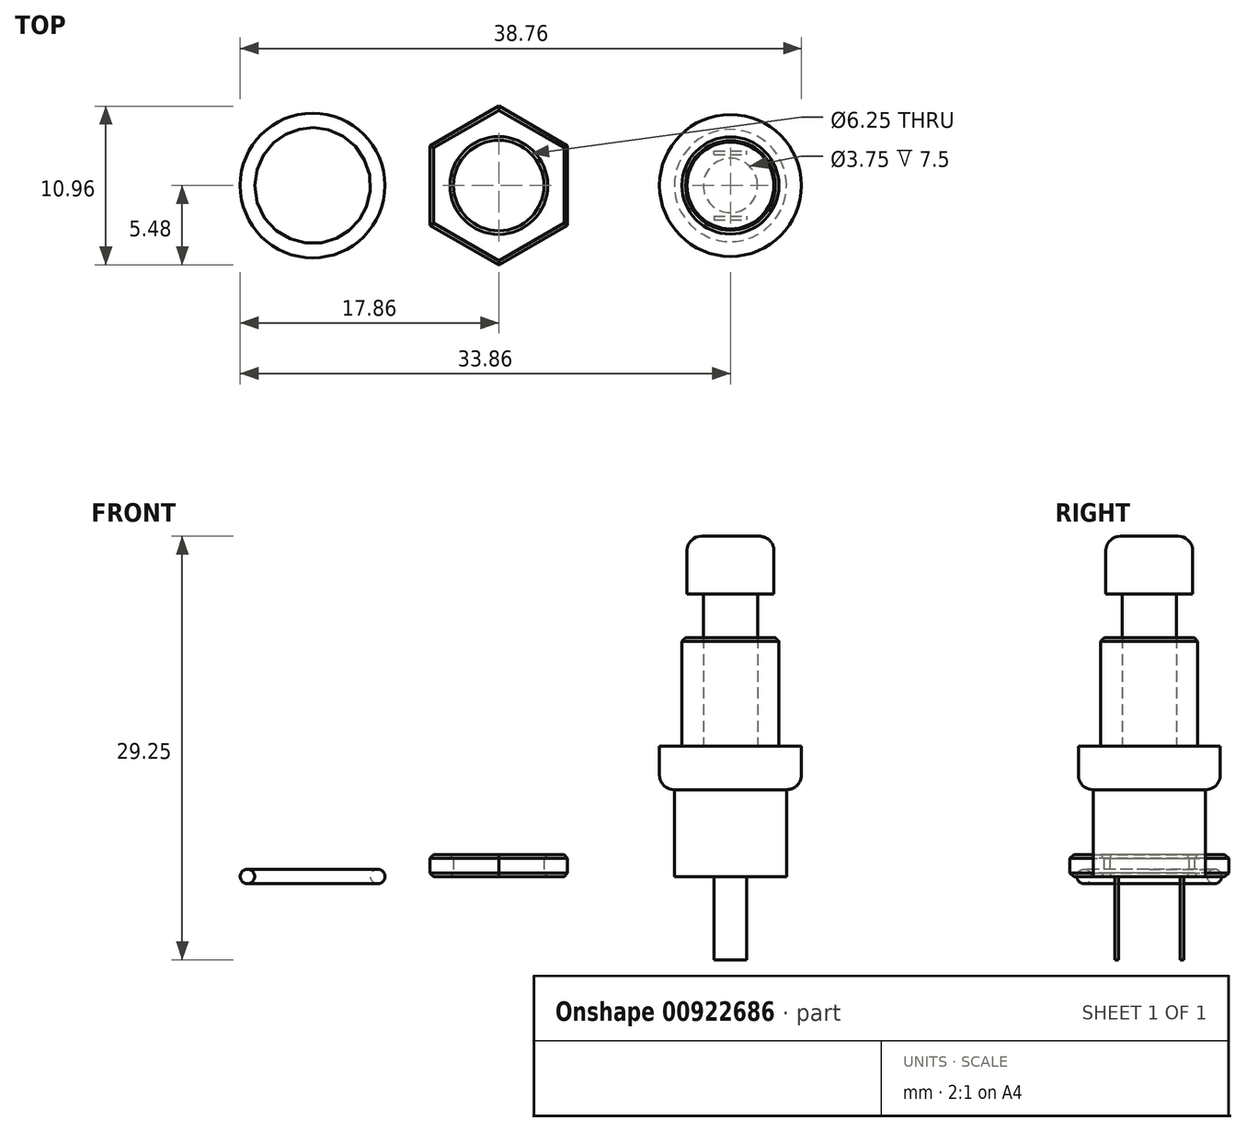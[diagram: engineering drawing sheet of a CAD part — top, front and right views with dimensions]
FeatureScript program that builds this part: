
annotation { "Feature Type Name" : "Feature", "Feature Type Description" : "" }
export const myFeature = defineFeature(function(context is Context, id is Id, definition is map)
    precondition{}
    {
        {
            var Q0;
            Q0=qCreatedBy(makeId("Top.planeOp"),FACE);
            var sketch = newSketch(context, id + "F0", { "sketchPlane" : qUnion([Q0])});
            skCircle(sketch, "E0", {"center": v(0, 0) * mm, "radius": 3.88 * mm});
            skCircle(sketch, "E1", {"center": v(0, 0) * mm, "radius": 4.9 * mm});
            skCircle(sketch, "E2", {"center": v(0, 0) * mm, "radius": 3.35 * mm});
            skCircle(sketch, "E3", {"center": v(0, 0) * mm, "radius": 1.88 * mm});
            skCircle(sketch, "E4", {"center": v(0, 0) * mm, "radius": 3 * mm});
            skLineSegment(sketch, "E5.bottom", {"start": v(-1.12, 2.12) * mm, "end": v(1.13, 2.12) * mm});
            skLineSegment(sketch, "E5.top", {"start": v(-1.12, 2.38) * mm, "end": v(1.12, 2.38) * mm});
            skLineSegment(sketch, "E5.left", {"start": v(-1.12, 2.12) * mm, "end": v(-1.12, 2.38) * mm});
            skLineSegment(sketch, "E5.right", {"start": v(1.13, 2.13) * mm, "end": v(1.13, 2.38) * mm});
            skPoint(sketch, "E5.middle", {"position": v(0, 2.25) * mm});
            skLineSegment(sketch, "E6.MirrorCS", {"start": v(-1.12, -2.12) * mm, "end": v(1.13, -2.12) * mm});
            skLineSegment(sketch, "E7.MirrorCS", {"start": v(1.13, -2.12) * mm, "end": v(1.13, -2.38) * mm});
            skLineSegment(sketch, "E8.MirrorCS", {"start": v(-1.12, -2.38) * mm, "end": v(1.12, -2.38) * mm});
            skLineSegment(sketch, "E9.MirrorCS", {"start": v(-1.12, -2.12) * mm, "end": v(-1.12, -2.38) * mm});
            skSolve(sketch);
        }
        {
            var Q0;
            Q0=makeQuery(id+"F0.imprint","IMPRINT",FACE,{"disambiguationData":[TD([[makeQuery(id+"F0.imprint","IMPRINT",EDGE,{"derivedFrom":sQuery(id+"F0.wireOp",EDGE,"E0")}),1.0]])]});
            var Q1;
            Q1=makeQuery(id+"F0.imprint","IMPRINT",FACE,{"disambiguationData":[TD([[makeQuery(id+"F0.imprint","IMPRINT",EDGE,{"derivedFrom":sQuery(id+"F0.wireOp",EDGE,"E2")}),1.0]])]});
            var Q2;
            Q2=makeQuery(id+"F0.imprint","IMPRINT",FACE,{"disambiguationData":[TD([[makeQuery(id+"F0.imprint","IMPRINT",EDGE,{"derivedFrom":sQuery(id+"F0.wireOp",EDGE,"E3")}),-1.0]])]});
            var Q3;
            Q3=makeQuery(id+"F0.imprint","IMPRINT",FACE,{"disambiguationData":[TD([[makeQuery(id+"F0.imprint","IMPRINT",EDGE,{"derivedFrom":sQuery(id+"F0.wireOp",EDGE,"E3")}),1.0]])]});
            var Q4;
            Q4=makeQuery(id+"F0.imprint","IMPRINT",FACE,{"disambiguationData":[TD([[makeQuery(id+"F0.imprint","IMPRINT",EDGE,{"derivedFrom":sQuery(id+"F0.wireOp",EDGE,"E5.bottom")}),1.0]])]});
            var Q5;
            Q5=makeQuery(id+"F0.imprint","IMPRINT",FACE,{"disambiguationData":[TD([[makeQuery(id+"F0.imprint","IMPRINT",EDGE,{"derivedFrom":sQuery(id+"F0.wireOp",EDGE,"E6.MirrorCS")}),-1.0]])]});
            extrude(context, id + "F1", {"entities" : qUnion([Q0, Q1, Q2, Q3, Q4, Q5]), "depth" : 6.5 * mm, "offsetDistance" : 25 * mm});
        }
        {
            var Q0;
            Q0=makeQuery(id+"F0.imprint","IMPRINT",FACE,{"disambiguationData":[TD([[makeQuery(id+"F0.imprint","IMPRINT",EDGE,{"derivedFrom":sQuery(id+"F0.wireOp",EDGE,"E0")}),1.0]])]});
            var Q1;
            Q1=makeQuery(id+"F0.imprint","IMPRINT",FACE,{"disambiguationData":[TD([[makeQuery(id+"F0.imprint","IMPRINT",EDGE,{"derivedFrom":sQuery(id+"F0.wireOp",EDGE,"E0")}),-1.0]])]});
            var Q2;
            Q2=makeQuery(id+"F0.imprint","IMPRINT",FACE,{"disambiguationData":[TD([[makeQuery(id+"F0.imprint","IMPRINT",EDGE,{"derivedFrom":sQuery(id+"F0.wireOp",EDGE,"E2")}),1.0]])]});
            var Q3;
            Q3=makeQuery(id+"F0.imprint","IMPRINT",FACE,{"disambiguationData":[TD([[makeQuery(id+"F0.imprint","IMPRINT",EDGE,{"derivedFrom":sQuery(id+"F0.wireOp",EDGE,"E3")}),-1.0]])]});
            var Q4;
            Q4=makeQuery(id+"F0.imprint","IMPRINT",FACE,{"disambiguationData":[TD([[makeQuery(id+"F0.imprint","IMPRINT",EDGE,{"derivedFrom":sQuery(id+"F0.wireOp",EDGE,"E3")}),1.0]])]});
            extrude(context, id + "F2", {"entities" : qUnion([Q0, Q1, Q2, Q3, Q4]), "depth" : (6 + 3) * mm, "offsetDistance" : 25 * mm, "hasSecondDirection" : true, "secondDirectionOppositeDirection" : false, "secondDirectionDepth" : 6 * mm});
        }
        {
            var Q0;
            Q0=makeQuery(id+"F0.imprint","IMPRINT",FACE,{"disambiguationData":[TD([[makeQuery(id+"F0.imprint","IMPRINT",EDGE,{"derivedFrom":sQuery(id+"F0.wireOp",EDGE,"E2")}),1.0]])]});
            var Q1;
            Q1=makeQuery(id+"F0.imprint","IMPRINT",FACE,{"disambiguationData":[TD([[makeQuery(id+"F0.imprint","IMPRINT",EDGE,{"derivedFrom":sQuery(id+"F0.wireOp",EDGE,"E3")}),-1.0]])]});
            var Q2;
            Q2=makeQuery(id+"F0.imprint","IMPRINT",FACE,{"disambiguationData":[TD([[makeQuery(id+"F0.imprint","IMPRINT",EDGE,{"derivedFrom":sQuery(id+"F0.wireOp",EDGE,"E5.bottom")}),1.0]])]});
            var Q3;
            Q3=makeQuery(id+"F0.imprint","IMPRINT",FACE,{"disambiguationData":[TD([[makeQuery(id+"F0.imprint","IMPRINT",EDGE,{"derivedFrom":sQuery(id+"F0.wireOp",EDGE,"E6.MirrorCS")}),-1.0]])]});
            extrude(context, id + "F3", {"entities" : qUnion([Q0, Q1, Q2, Q3]), "operationType" : NewBodyOperationType.ADD, "depth" : 16.5 * mm, "offsetDistance" : 25 * mm, "hasSecondDirection" : true, "secondDirectionOppositeDirection" : false, "secondDirectionDepth" : 6 * mm});
        }
        {
            var Q0;
            Q0=makeQuery(id+"F0.imprint","IMPRINT",FACE,{"disambiguationData":[TD([[makeQuery(id+"F0.imprint","IMPRINT",EDGE,{"derivedFrom":sQuery(id+"F0.wireOp",EDGE,"E3")}),1.0]])]});
            extrude(context, id + "F4", {"entities" : qUnion([Q0]), "depth" : 23.5 * mm, "offsetDistance" : 25 * mm, "hasSecondDirection" : true, "secondDirectionOppositeDirection" : false, "secondDirectionDepth" : 16.5 * mm});
        }
        {
            var Q0;
            Q0=makeQuery(id+"F0.imprint","IMPRINT",FACE,{"disambiguationData":[TD([[makeQuery(id+"F0.imprint","IMPRINT",EDGE,{"derivedFrom":sQuery(id+"F0.wireOp",EDGE,"E3")}),1.0]])]});
            var Q1;
            Q1=makeQuery(id+"F0.imprint","IMPRINT",FACE,{"disambiguationData":[TD([[makeQuery(id+"F0.imprint","IMPRINT",EDGE,{"derivedFrom":sQuery(id+"F0.wireOp",EDGE,"E6.MirrorCS")}),-1.0]])]});
            var Q2;
            Q2=makeQuery(id+"F0.imprint","IMPRINT",FACE,{"disambiguationData":[TD([[makeQuery(id+"F0.imprint","IMPRINT",EDGE,{"derivedFrom":sQuery(id+"F0.wireOp",EDGE,"E5.bottom")}),1.0]])]});
            var Q3;
            Q3=makeQuery(id+"F0.imprint","IMPRINT",FACE,{"disambiguationData":[TD([[makeQuery(id+"F0.imprint","IMPRINT",EDGE,{"derivedFrom":sQuery(id+"F0.wireOp",EDGE,"E3")}),-1.0]])]});
            extrude(context, id + "F5", {"entities" : qUnion([Q0, Q1, Q2, Q3]), "operationType" : NewBodyOperationType.ADD, "depth" : 23.5 * mm, "offsetDistance" : 25 * mm, "hasSecondDirection" : true, "secondDirectionOppositeDirection" : false, "secondDirectionDepth" : (23.5 - 4) * mm});
        }
        {
            var Q0;
            Q0=makeQuery(id+"F5.opExtrude","CAP_EDGE",EDGE,{"disambiguationData":[OSD([sQuery(id+"F0.wireOp",EDGE,"E4")])],"isStart":false});
            fillet(context, id + "F6", {"entities" : qUnion([Q0]), "radius" : 1 * mm, "tangentPropagation" : true, "allowEdgeOverflow" : false});
        }
        {
            var Q0;
            Q0=makeQuery(id+"F2.opExtrude","CAP_EDGE",EDGE,{"disambiguationData":[OSD([sQuery(id+"F0.wireOp",EDGE,"E1")])],"isStart":true});
            fillet(context, id + "F7", {"entities" : qUnion([Q0]), "radius" : 1 * mm, "tangentPropagation" : true, "allowEdgeOverflow" : false});
        }
        {
            var Q0;
            Q0=makeQuery(id+"F3.opExtrude","CAP_EDGE",EDGE,{"disambiguationData":[OSD([sQuery(id+"F0.wireOp",EDGE,"E2")])],"isStart":false});
            chamfer(context, id + "F8", {"entities" : qUnion([Q0]), "width" : .25 * mm, "tangentPropagation" : true});
        }
        {
            var Q0;
            Q0=makeQuery(id+"F0.imprint","IMPRINT",FACE,{"disambiguationData":[TD([[makeQuery(id+"F0.imprint","IMPRINT",EDGE,{"derivedFrom":sQuery(id+"F0.wireOp",EDGE,"E5.bottom")}),1.0]])]});
            var Q1;
            Q1=makeQuery(id+"F0.imprint","IMPRINT",FACE,{"disambiguationData":[TD([[makeQuery(id+"F0.imprint","IMPRINT",EDGE,{"derivedFrom":sQuery(id+"F0.wireOp",EDGE,"E6.MirrorCS")}),-1.0]])]});
            extrude(context, id + "F9", {"entities" : qUnion([Q0, Q1]), "operationType" : NewBodyOperationType.ADD, "oppositeDirection" : true, "depth" : 5.75 * mm, "offsetDistance" : 25 * mm});
        }
        {
            var Q0;
            Q0=qCreatedBy(makeId("Top.planeOp"),FACE);
            var sketch = newSketch(context, id + "F10", { "sketchPlane" : qUnion([Q0])});
            skCircle(sketch, "E10", {"center": v(-16, 0) * mm, "radius": 3.12 * mm});
            skCircle(sketch, "E11.cCircle", {"center": v(-16, 0) * mm, "radius": 4.75 * mm, "construction": true});
            skLineSegment(sketch, "E11.0", {"start": v(-20.75, -2.74) * mm, "end": v(-20.75, 2.74) * mm});
            skLineSegment(sketch, "E11.1", {"start": v(-20.75, 2.74) * mm, "end": v(-16, 5.48) * mm});
            skLineSegment(sketch, "E11.2", {"start": v(-16, 5.48) * mm, "end": v(-11.25, 2.74) * mm});
            skLineSegment(sketch, "E11.3", {"start": v(-11.25, 2.74) * mm, "end": v(-11.25, -2.74) * mm});
            skLineSegment(sketch, "E11.4", {"start": v(-11.25, -2.74) * mm, "end": v(-16, -5.48) * mm});
            skLineSegment(sketch, "E11.5", {"start": v(-16, -5.48) * mm, "end": v(-20.75, -2.74) * mm});
            skPoint(sketch, "E11.0.midPoint", {"position": v(-20.75, 0) * mm});
            skSolve(sketch);
        }
        {
            var Q0;
            Q0=makeQuery(id+"F10.imprint","IMPRINT",FACE,{"disambiguationData":[TD([[makeQuery(id+"F10.imprint","IMPRINT",EDGE,{"derivedFrom":sQuery(id+"F10.wireOp",EDGE,"E10")}),-1.0]])]});
            extrude(context, id + "F11", {"entities" : qUnion([Q0]), "depth" : 1.5 * mm, "offsetDistance" : 25 * mm});
        }
        {
            var Q0;
            Q0=makeQuery(id+"F11.opExtrude","CAP_FACE",FACE,{"disambiguationData":[OSD([sQuery(id+"F10.wireOp",EDGE,"E10"),sQuery(id+"F10.wireOp",EDGE,"E11.0"),sQuery(id+"F10.wireOp",EDGE,"E11.1"),sQuery(id+"F10.wireOp",EDGE,"E11.2"),sQuery(id+"F10.wireOp",EDGE,"E11.3"),sQuery(id+"F10.wireOp",EDGE,"E11.4"),sQuery(id+"F10.wireOp",EDGE,"E11.5")])],"isStart":false});
            var Q1;
            Q1=makeQuery(id+"F11.opExtrude","CAP_FACE",FACE,{"disambiguationData":[OSD([sQuery(id+"F10.wireOp",EDGE,"E10"),sQuery(id+"F10.wireOp",EDGE,"E11.0"),sQuery(id+"F10.wireOp",EDGE,"E11.1"),sQuery(id+"F10.wireOp",EDGE,"E11.2"),sQuery(id+"F10.wireOp",EDGE,"E11.3"),sQuery(id+"F10.wireOp",EDGE,"E11.4"),sQuery(id+"F10.wireOp",EDGE,"E11.5")])],"isStart":true});
            chamfer(context, id + "F12", {"entities" : qUnion([Q0, Q1]), "width" : .25 * mm, "tangentPropagation" : true});
        }
        {
            var Q0;
            Q0=qCreatedBy(makeId("Front.planeOp"),FACE);
            var sketch = newSketch(context, id + "F13", { "sketchPlane" : qUnion([Q0])});
            skCircle(sketch, "E12", {"center": v(-24.36, 0) * mm, "radius": 0.5 * mm});
            skSolve(sketch);
        }
        {
            var Q0;
            Q0=qCreatedBy(makeId("Top.planeOp"),FACE);
            var sketch = newSketch(context, id + "F14", { "sketchPlane" : qUnion([Q0])});
            skCircle(sketch, "E13", {"center": v(-28.86, 0) * mm, "radius": 4.5 * mm});
            skSolve(sketch);
        }
        {
            var Q0;
            Q0=makeQuery(id+"F13.imprint","IMPRINT",FACE,{"disambiguationData":[TD([[makeQuery(id+"F13.imprint","IMPRINT",EDGE,{"derivedFrom":sQuery(id+"F13.wireOp",EDGE,"E12")}),1.0]])]});
            var Q1;
            Q1=sQuery(id+"F14.wireOp",EDGE,"E13");
            revolve(context, id + "F15", {"surfaceOperationType" : NewSurfaceOperationType.NEW, "entities" : qUnion([Q0]), "axis" : qUnion([Q1]), "revolveType" : RevolveType.FULL});
        }
    });
